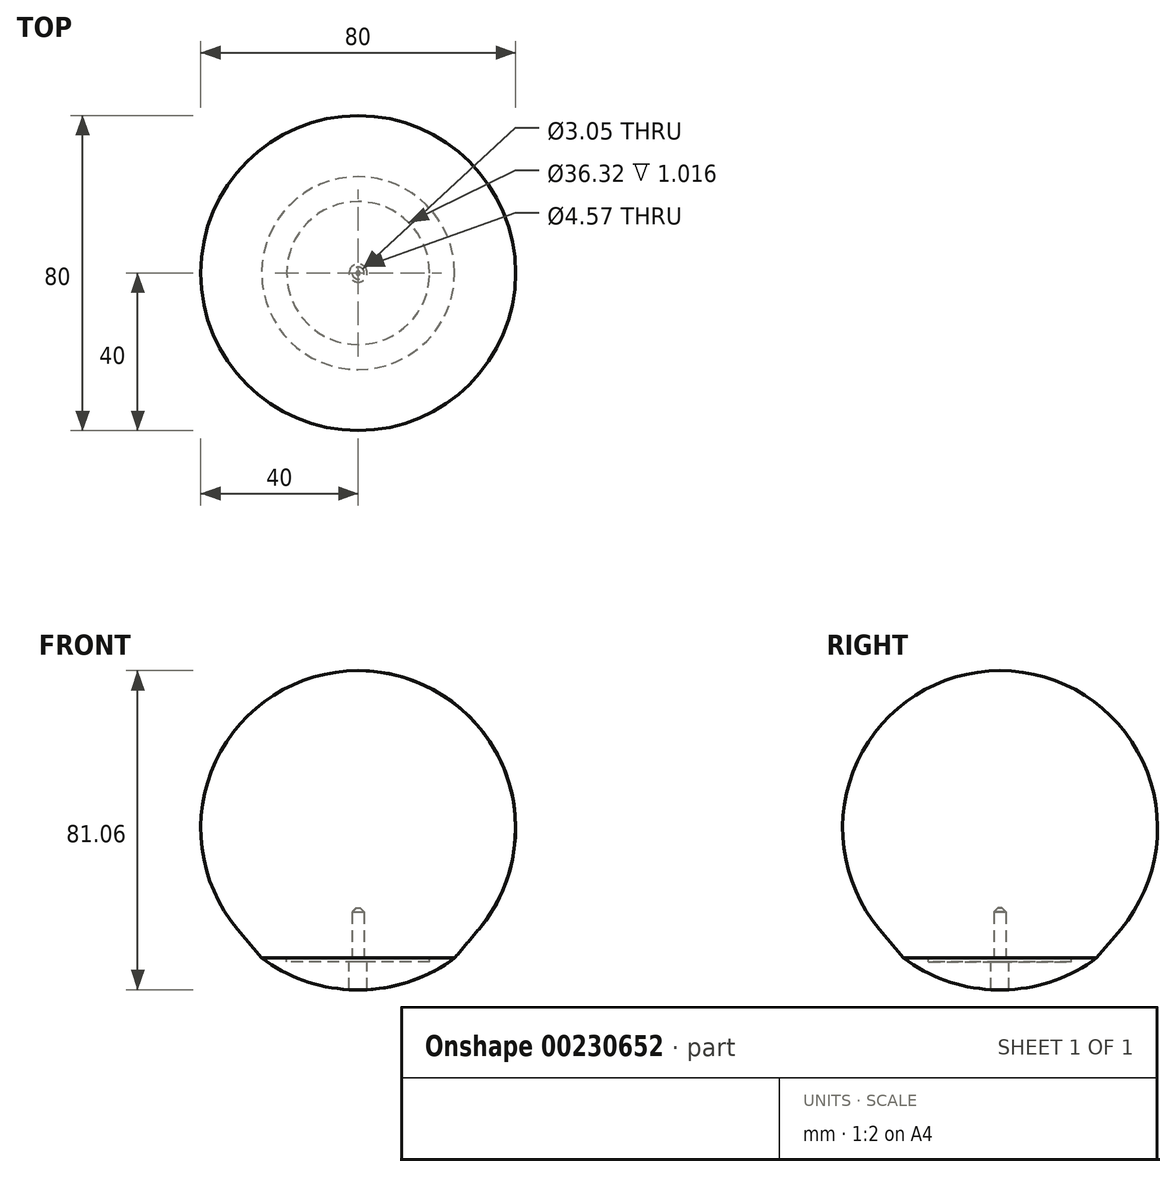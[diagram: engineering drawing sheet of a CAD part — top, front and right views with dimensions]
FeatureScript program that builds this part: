
annotation { "Feature Type Name" : "Feature", "Feature Type Description" : "" }
export const myFeature = defineFeature(function(context is Context, id is Id, definition is map)
    precondition{}
    {
        {
            var Q0;
            Q0=qCreatedBy(makeId("Front.planeOp"),FACE);
            var sketch = newSketch(context, id + "F0", { "sketchPlane" : qUnion([Q0])});
            skArc(sketch, "E0", {"start": v(30.64, 7.3) * mm, "mid": v(36.25, 49.92) * mm, "end": v(0, 73.02) * mm});
            skArc(sketch, "E1", {"start": v(25.34, 4.57) * mm, "mid": v(37.91, 36.8) * mm, "end": v(19.23, 65.91) * mm});
            skArc(sketch, "E2", {"start": v(19.23, 65.91) * mm, "mid": v(4.2, 36.17) * mm, "end": v(14.81, 4.57) * mm});
            skLineSegment(sketch, "E3", {"start": v(0, 73.02) * mm, "end": v(0, 0) * mm});
            skLineSegment(sketch, "E4", {"start": v(0, 0) * mm, "end": v(24.5, 0) * mm});
            skLineSegment(sketch, "E5", {"start": v(0, 0) * mm, "end": v(0, -57.5) * mm, "construction": true});
            skLineSegment(sketch, "E6", {"start": v(25.34, 4.57) * mm, "end": v(14.81, 4.57) * mm});
            skLineSegment(sketch, "E7", {"start": v(30.64, 7.3) * mm, "end": v(24.5, 0) * mm});
            skSolve(sketch);
        }
        {
            var Q0;
            Q0=makeQuery(id+"F0.imprint","IMPRINT",FACE,{"disambiguationData":[TD([[makeQuery(id+"F0.imprint","IMPRINT",EDGE,{"derivedFrom":sQuery(id+"F0.wireOp",EDGE,"E0")}),1.0]])]});
            var Q1;
            Q1=makeQuery(id+"F0.imprint","IMPRINT",FACE,{"disambiguationData":[TD([[makeQuery(id+"F0.imprint","IMPRINT",EDGE,{"derivedFrom":sQuery(id+"F0.wireOp",EDGE,"E1")}),1.0]])]});
            var Q2;
            Q2=sQuery(id+"F0.wireOp",EDGE,"E5");
            revolve(context, id + "F1", {"entities" : qUnion([Q0, Q1]), "axis" : qUnion([Q2]), "revolveType" : RevolveType.FULL});
        }
        {
            var Q0;
            Q0=makeQuery(id+"F1.opRevolve","SWEPT_FACE",FACE,{"disambiguationData":[OSD([sQuery(id+"F0.wireOp",EDGE,"E4")])]});
            var sketch = newSketch(context, id + "F2", { "sketchPlane" : qUnion([Q0])});
            skCircle(sketch, "E8", {"center": v(0, 0) * mm, "radius": 1.52 * mm});
            skSolve(sketch);
        }
        {
            var Q0;
            Q0 = qSketchRegion(id + "F2", true);
            extrude(context, id + "F3", {"entities" : qUnion([Q0]), "operationType" : NewBodyOperationType.REMOVE, "oppositeDirection" : true, "depth" : 12.7 * mm});
        }
        {
            var Q0;
            Q0=makeQuery(id+"F3.boolean.opBoolean","COPY",EDGE,{"derivedFrom":makeQuery(id+"F3.opExtrude","CAP_EDGE",EDGE,{"disambiguationData":[OSD([sQuery(id+"F2.wireOp",EDGE,"E8")])],"isStart":false})});
            chamfer(context, id + "F4", {"entities" : qUnion([Q0]), "width" : 1.02 * mm, "tangentPropagation" : true});
        }
        {
            var Q0;
            Q0=qCreatedBy(makeId("Front.planeOp"),FACE);
            var sketch = newSketch(context, id + "F5", { "sketchPlane" : qUnion([Q0])});
            skArc(sketch, "E9", {"start": v(0, -8.1) * mm, "mid": v(12.9, -6.02) * mm, "end": v(24.5, 0) * mm});
            skLineSegment(sketch, "E10", {"start": v(24.5, 0) * mm, "end": v(18.16, 0) * mm});
            skLineSegment(sketch, "E11", {"start": v(18.16, 0) * mm, "end": v(18.16, -1.02) * mm});
            skLineSegment(sketch, "E12", {"start": v(18.16, -1.02) * mm, "end": v(0, -1.02) * mm});
            skLineSegment(sketch, "E13", {"start": v(0, -1.02) * mm, "end": v(0, -8.1) * mm});
            skSolve(sketch);
        }
        {
            var Q0;
            Q0 = qSketchRegion(id + "F5", true);
            var Q1;
            Q1=sQuery(id+"F0.wireOp",EDGE,"E5");
            revolve(context, id + "F6", {"entities" : qUnion([Q0]), "axis" : qUnion([Q1]), "revolveType" : RevolveType.FULL});
        }
        {
            var Q0;
            Q0=makeQuery(id+"F6.opRevolve","SWEPT_FACE",FACE,{"disambiguationData":[OSD([sQuery(id+"F5.wireOp",EDGE,"E12")])]});
            var sketch = newSketch(context, id + "F7", { "sketchPlane" : qUnion([Q0])});
            skCircle(sketch, "E14", {"center": v(0, 0) * mm, "radius": 2.29 * mm});
            skSolve(sketch);
        }
        {
            var Q0;
            Q0 = qSketchRegion(id + "F7", true);
            extrude(context, id + "F8", {"entities" : qUnion([Q0]), "operationType" : NewBodyOperationType.REMOVE, "oppositeDirection" : true, "depth" : 25.4 * mm});
        }
    });
